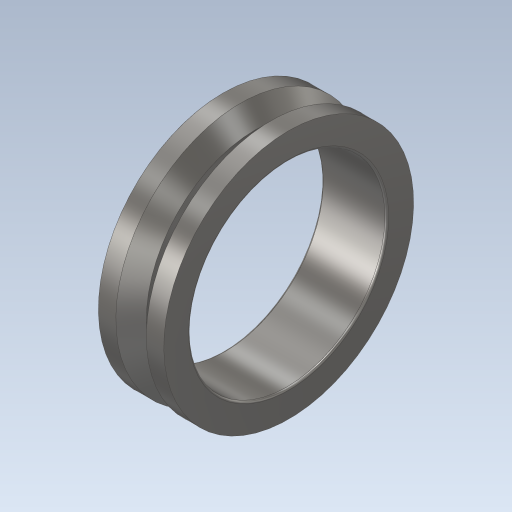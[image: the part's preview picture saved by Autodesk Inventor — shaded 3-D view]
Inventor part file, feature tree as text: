
AUTODESK INVENTOR PART (.ipt)
format: ipt  version: 2024 (Build 280153000, 153)  size: 180,736 bytes
history: native  units: mm
features: revolve x2, sketch x2
ambient origin geometry x8: Origin, YZ Plane, XZ Plane, XY Plane, X Axis, Y Axis, Z Axis, Center Point
bodies: Solid1 (feature_tree)
feature tree (4):
  revolve  "Revolution1"  Angle=360.0deg
  revolve  "Revolution2"  [1 undecoded]
  sketch  "Sketch_1"  dims[d0=360.0deg d1=360.0deg]
  sketch  "Sketch_2"
note: 1 required parameter value undecoded (feature->parameter linkage not recoverable at this tier; creation-order binding heuristic only, values carry confidence <= 0.55)
